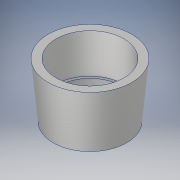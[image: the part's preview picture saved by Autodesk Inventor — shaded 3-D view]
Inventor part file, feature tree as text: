
AUTODESK INVENTOR PART (.ipt)
format: ipt  version: 2017 SP1 (Build 210196100, 196)  size: 150,528 bytes
history: native  units: in
note: dims shown in document units (in); Inventor stores cm internally (conversion verified against a paired STEP export)
features: revolve x1, sketch x1
ambient origin geometry x8: Origin, YZ Plane, XZ Plane, XY Plane, X Axis, Y Axis, Z Axis, Center Point
bodies: Solid1 (feature_tree)
feature tree (2):
  revolve  "Revolution1"  [1 undecoded]
  sketch  "Sketch1"  dims[d0=0.5in d1=1.13in d3=15.0deg d4=0.25in d9=1.5in d11=0.5in d13=3.75in d14=0.25in d15=1.0in d16=0.25in d17=0.5in d18=0.234in d19=0.234in d20=0.5in d22=4.25in d23=2.5in d25=1.0in d26=0.25in d27=5.25in d28=0.125in d29=4.0in d30=0.25in d31=0.1718in d32=1.75in d33=0.125in d34=0.801in d35=0.375in d37=90.0deg]
note: 1 required parameter value undecoded (feature->parameter linkage not recoverable at this tier; creation-order binding heuristic only, values carry confidence <= 0.55)
